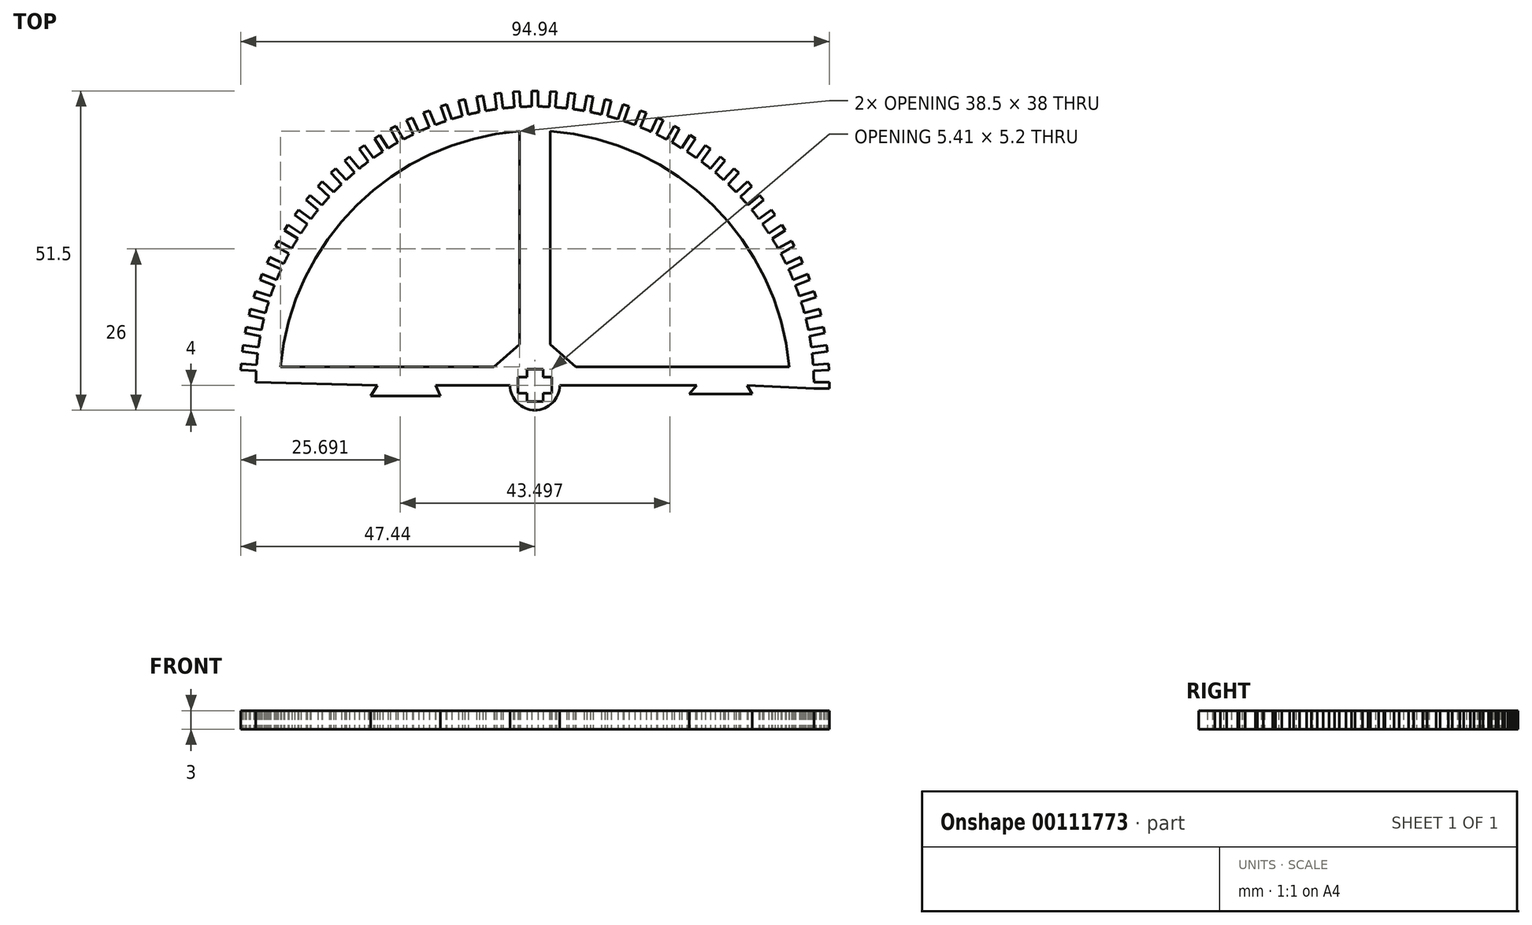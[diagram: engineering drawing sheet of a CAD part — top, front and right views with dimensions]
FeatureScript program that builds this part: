
annotation { "Feature Type Name" : "Feature", "Feature Type Description" : "" }
export const myFeature = defineFeature(function(context is Context, id is Id, definition is map)
    precondition{}
    {
        {
            var Q0;
            Q0=qCreatedBy(makeId("Top.planeOp"),FACE);
            var sketch = newSketch(context, id + "F0", { "sketchPlane" : qUnion([Q0])});
            skArc(sketch, "E0", {"start": v(-4, 0) * mm, "mid": v(0, -4) * mm, "end": v(4, 0) * mm});
            skLineSegment(sketch, "E1", {"start": v(-4, 0) * mm, "end": v(-16, 0) * mm});
            skLineSegment(sketch, "E2", {"start": v(-16, 0) * mm, "end": v(-15.27, -1.74) * mm});
            skLineSegment(sketch, "E3", {"start": v(-15.27, -1.74) * mm, "end": v(-26.47, -1.74) * mm});
            skLineSegment(sketch, "E4", {"start": v(-45, 0.5) * mm, "end": v(-25.37, 0) * mm});
            skLineSegment(sketch, "E5", {"start": v(-25.37, 0) * mm, "end": v(-26.47, -1.74) * mm});
            skLineSegment(sketch, "E6", {"start": v(45, -0.5) * mm, "end": v(34.22, 0) * mm});
            skLineSegment(sketch, "E7", {"start": v(34.22, 0) * mm, "end": v(35.03, -1.4) * mm});
            skLineSegment(sketch, "E8", {"start": v(35.03, -1.4) * mm, "end": v(24.89, -1.4) * mm});
            skLineSegment(sketch, "E9", {"start": v(24.89, -1.4) * mm, "end": v(26.1, 0) * mm});
            skLineSegment(sketch, "E10", {"start": v(26.1, 0) * mm, "end": v(4, 0) * mm});
            skArc(sketch, "E11", {"start": v(45, -0.5) * mm, "mid": v(0.5, 45) * mm, "end": v(-45, 0.5) * mm});
            skLineSegment(sketch, "E12.MirrorCS", {"start": v(-6.6, 3) * mm, "end": v(-41, 3) * mm});
            skLineSegment(sketch, "E13.MirrorCS", {"start": v(-2.5, 6.6) * mm, "end": v(-6.6, 3) * mm});
            skLineSegment(sketch, "E14.MirrorCS", {"start": v(-2.5, 6.6) * mm, "end": v(-2.5, 41) * mm});
            skArc(sketch, "E15.MirrorCS", {"start": v(-41, 3) * mm, "mid": v(-28.72, 29.07) * mm, "end": v(-2.5, 41) * mm});
            skLineSegment(sketch, "E16.MirrorCS", {"start": v(2.5, 6.6) * mm, "end": v(2.5, 41) * mm});
            skArc(sketch, "E17.MirrorCS", {"start": v(41, 3) * mm, "mid": v(28.72, 29.07) * mm, "end": v(2.5, 41) * mm});
            skLineSegment(sketch, "E18.MirrorCS", {"start": v(6.6, 3) * mm, "end": v(41, 3) * mm});
            skLineSegment(sketch, "E19.MirrorCS", {"start": v(2.5, 6.6) * mm, "end": v(6.6, 3) * mm});
            skLineSegment(sketch, "E20.1.50.0", {"start": v(47.5, 0.5) * mm, "end": v(45, 0.5) * mm});
            skLineSegment(sketch, "E20.3.50.0", {"start": v(47.5, -0.5) * mm, "end": v(45, -0.5) * mm});
            skLineSegment(sketch, "E20.6.50.0", {"start": v(47.5, 0) * mm, "end": v(47.5, -0.5) * mm});
            skLineSegment(sketch, "E20.9.50.0", {"start": v(47.5, 0) * mm, "end": v(47.5, 0.5) * mm});
            skLineSegment(sketch, "E20.1.51.0", {"start": v(47.37, 3.48) * mm, "end": v(44.88, 3.32) * mm});
            skLineSegment(sketch, "E20.3.51.0", {"start": v(47.44, 2.48) * mm, "end": v(44.94, 2.33) * mm});
            skLineSegment(sketch, "E20.6.51.0", {"start": v(47.4, 2.98) * mm, "end": v(47.44, 2.48) * mm});
            skLineSegment(sketch, "E20.9.51.0", {"start": v(47.4, 2.98) * mm, "end": v(47.37, 3.48) * mm});
            skLineSegment(sketch, "E20.1.52.0", {"start": v(47.06, 6.45) * mm, "end": v(44.58, 6.14) * mm});
            skLineSegment(sketch, "E20.3.52.0", {"start": v(47.19, 5.46) * mm, "end": v(44.7, 5.14) * mm});
            skLineSegment(sketch, "E20.6.52.0", {"start": v(47.13, 5.95) * mm, "end": v(47.19, 5.46) * mm});
            skLineSegment(sketch, "E20.9.52.0", {"start": v(47.13, 5.95) * mm, "end": v(47.06, 6.45) * mm});
            skLineSegment(sketch, "E20.1.53.0", {"start": v(46.56, 9.4) * mm, "end": v(44.1, 8.92) * mm});
            skLineSegment(sketch, "E20.3.53.0", {"start": v(46.75, 8.4) * mm, "end": v(44.3, 7.94) * mm});
            skLineSegment(sketch, "E20.6.53.0", {"start": v(46.66, 8.9) * mm, "end": v(46.75, 8.4) * mm});
            skLineSegment(sketch, "E20.9.53.0", {"start": v(46.66, 8.9) * mm, "end": v(46.56, 9.4) * mm});
            skLineSegment(sketch, "E20.1.54.0", {"start": v(45.88, 12.3) * mm, "end": v(43.46, 11.67) * mm});
            skLineSegment(sketch, "E20.3.54.0", {"start": v(46.13, 11.33) * mm, "end": v(43.7, 10.7) * mm});
            skLineSegment(sketch, "E20.6.54.0", {"start": v(46, 11.81) * mm, "end": v(46.13, 11.33) * mm});
            skLineSegment(sketch, "E20.9.54.0", {"start": v(46, 11.81) * mm, "end": v(45.88, 12.3) * mm});
            skLineSegment(sketch, "E20.1.55.0", {"start": v(45.02, 15.15) * mm, "end": v(42.64, 14.38) * mm});
            skLineSegment(sketch, "E20.3.55.0", {"start": v(45.33, 14.2) * mm, "end": v(42.95, 13.43) * mm});
            skLineSegment(sketch, "E20.6.55.0", {"start": v(45.18, 14.68) * mm, "end": v(45.33, 14.2) * mm});
            skLineSegment(sketch, "E20.9.55.0", {"start": v(45.18, 14.68) * mm, "end": v(45.02, 15.15) * mm});
            skLineSegment(sketch, "E20.1.56.0", {"start": v(43.98, 17.95) * mm, "end": v(41.65, 17.03) * mm});
            skLineSegment(sketch, "E20.3.56.0", {"start": v(44.35, 17.02) * mm, "end": v(42.02, 16.1) * mm});
            skLineSegment(sketch, "E20.6.56.0", {"start": v(44.16, 17.49) * mm, "end": v(44.35, 17.02) * mm});
            skLineSegment(sketch, "E20.9.56.0", {"start": v(44.16, 17.49) * mm, "end": v(43.98, 17.95) * mm});
            skLineSegment(sketch, "E20.1.57.0", {"start": v(42.77, 20.68) * mm, "end": v(40.5, 19.61) * mm});
            skLineSegment(sketch, "E20.3.57.0", {"start": v(43.2, 19.77) * mm, "end": v(40.93, 18.7) * mm});
            skLineSegment(sketch, "E20.6.57.0", {"start": v(42.98, 20.22) * mm, "end": v(43.2, 19.77) * mm});
            skLineSegment(sketch, "E20.9.57.0", {"start": v(42.98, 20.22) * mm, "end": v(42.77, 20.68) * mm});
            skLineSegment(sketch, "E20.1.58.0", {"start": v(41.38, 23.32) * mm, "end": v(39.2, 22.12) * mm});
            skLineSegment(sketch, "E20.3.58.0", {"start": v(41.87, 22.45) * mm, "end": v(39.67, 21.24) * mm});
            skLineSegment(sketch, "E20.6.58.0", {"start": v(41.62, 22.88) * mm, "end": v(41.87, 22.45) * mm});
            skLineSegment(sketch, "E20.9.58.0", {"start": v(41.62, 22.88) * mm, "end": v(41.38, 23.32) * mm});
            skLineSegment(sketch, "E20.1.59.0", {"start": v(39.84, 25.87) * mm, "end": v(37.72, 24.53) * mm});
            skLineSegment(sketch, "E20.3.59.0", {"start": v(40.37, 25.03) * mm, "end": v(38.26, 23.69) * mm});
            skLineSegment(sketch, "E20.6.59.0", {"start": v(40.1, 25.45) * mm, "end": v(40.37, 25.03) * mm});
            skLineSegment(sketch, "E20.9.59.0", {"start": v(40.1, 25.45) * mm, "end": v(39.84, 25.87) * mm});
            skLineSegment(sketch, "E20.1.60.0", {"start": v(38.13, 28.32) * mm, "end": v(36.1, 26.85) * mm});
            skLineSegment(sketch, "E20.3.60.0", {"start": v(38.72, 27.52) * mm, "end": v(36.7, 26.04) * mm});
            skLineSegment(sketch, "E20.6.60.0", {"start": v(38.43, 27.92) * mm, "end": v(38.72, 27.52) * mm});
            skLineSegment(sketch, "E20.9.60.0", {"start": v(38.43, 27.92) * mm, "end": v(38.13, 28.32) * mm});
            skLineSegment(sketch, "E20.1.61.0", {"start": v(36.28, 30.66) * mm, "end": v(34.35, 29.07) * mm});
            skLineSegment(sketch, "E20.3.61.0", {"start": v(36.92, 29.9) * mm, "end": v(34.99, 28.3) * mm});
            skLineSegment(sketch, "E20.6.61.0", {"start": v(36.6, 30.28) * mm, "end": v(36.92, 29.9) * mm});
            skLineSegment(sketch, "E20.9.61.0", {"start": v(36.6, 30.28) * mm, "end": v(36.28, 30.66) * mm});
            skLineSegment(sketch, "E20.1.62.0", {"start": v(34.28, 32.88) * mm, "end": v(32.46, 31.17) * mm});
            skLineSegment(sketch, "E20.3.62.0", {"start": v(34.97, 32.15) * mm, "end": v(33.14, 30.44) * mm});
            skLineSegment(sketch, "E20.6.62.0", {"start": v(34.63, 32.52) * mm, "end": v(34.97, 32.15) * mm});
            skLineSegment(sketch, "E20.9.62.0", {"start": v(34.63, 32.52) * mm, "end": v(34.28, 32.88) * mm});
            skLineSegment(sketch, "E20.1.63.0", {"start": v(32.15, 34.97) * mm, "end": v(30.44, 33.14) * mm});
            skLineSegment(sketch, "E20.3.63.0", {"start": v(32.88, 34.28) * mm, "end": v(31.17, 32.46) * mm});
            skLineSegment(sketch, "E20.6.63.0", {"start": v(32.52, 34.63) * mm, "end": v(32.88, 34.28) * mm});
            skLineSegment(sketch, "E20.9.63.0", {"start": v(32.52, 34.63) * mm, "end": v(32.15, 34.97) * mm});
            skLineSegment(sketch, "E20.1.64.0", {"start": v(29.9, 36.92) * mm, "end": v(28.3, 34.99) * mm});
            skLineSegment(sketch, "E20.3.64.0", {"start": v(30.66, 36.28) * mm, "end": v(29.07, 34.35) * mm});
            skLineSegment(sketch, "E20.6.64.0", {"start": v(30.28, 36.6) * mm, "end": v(30.66, 36.28) * mm});
            skLineSegment(sketch, "E20.9.64.0", {"start": v(30.28, 36.6) * mm, "end": v(29.9, 36.92) * mm});
            skLineSegment(sketch, "E20.1.65.0", {"start": v(27.52, 38.72) * mm, "end": v(26.04, 36.7) * mm});
            skLineSegment(sketch, "E20.3.65.0", {"start": v(28.32, 38.13) * mm, "end": v(26.85, 36.1) * mm});
            skLineSegment(sketch, "E20.6.65.0", {"start": v(27.92, 38.43) * mm, "end": v(28.32, 38.13) * mm});
            skLineSegment(sketch, "E20.9.65.0", {"start": v(27.92, 38.43) * mm, "end": v(27.52, 38.72) * mm});
            skLineSegment(sketch, "E20.1.66.0", {"start": v(25.03, 40.37) * mm, "end": v(23.69, 38.26) * mm});
            skLineSegment(sketch, "E20.3.66.0", {"start": v(25.87, 39.84) * mm, "end": v(24.53, 37.72) * mm});
            skLineSegment(sketch, "E20.6.66.0", {"start": v(25.45, 40.1) * mm, "end": v(25.87, 39.84) * mm});
            skLineSegment(sketch, "E20.9.66.0", {"start": v(25.45, 40.1) * mm, "end": v(25.03, 40.37) * mm});
            skLineSegment(sketch, "E20.1.67.0", {"start": v(22.45, 41.87) * mm, "end": v(21.24, 39.67) * mm});
            skLineSegment(sketch, "E20.3.67.0", {"start": v(23.32, 41.38) * mm, "end": v(22.12, 39.2) * mm});
            skLineSegment(sketch, "E20.6.67.0", {"start": v(22.88, 41.62) * mm, "end": v(23.32, 41.38) * mm});
            skLineSegment(sketch, "E20.9.67.0", {"start": v(22.88, 41.62) * mm, "end": v(22.45, 41.87) * mm});
            skLineSegment(sketch, "E20.1.68.0", {"start": v(19.77, 43.2) * mm, "end": v(18.7, 40.93) * mm});
            skLineSegment(sketch, "E20.3.68.0", {"start": v(20.68, 42.77) * mm, "end": v(19.61, 40.5) * mm});
            skLineSegment(sketch, "E20.6.68.0", {"start": v(20.22, 42.98) * mm, "end": v(20.68, 42.77) * mm});
            skLineSegment(sketch, "E20.9.68.0", {"start": v(20.22, 42.98) * mm, "end": v(19.77, 43.2) * mm});
            skLineSegment(sketch, "E20.1.69.0", {"start": v(17.02, 44.35) * mm, "end": v(16.1, 42.02) * mm});
            skLineSegment(sketch, "E20.3.69.0", {"start": v(17.95, 43.98) * mm, "end": v(17.03, 41.65) * mm});
            skLineSegment(sketch, "E20.6.69.0", {"start": v(17.49, 44.16) * mm, "end": v(17.95, 43.98) * mm});
            skLineSegment(sketch, "E20.9.69.0", {"start": v(17.49, 44.16) * mm, "end": v(17.02, 44.35) * mm});
            skLineSegment(sketch, "E20.1.70.0", {"start": v(14.2, 45.33) * mm, "end": v(13.43, 42.95) * mm});
            skLineSegment(sketch, "E20.3.70.0", {"start": v(15.15, 45.02) * mm, "end": v(14.38, 42.64) * mm});
            skLineSegment(sketch, "E20.6.70.0", {"start": v(14.68, 45.18) * mm, "end": v(15.15, 45.02) * mm});
            skLineSegment(sketch, "E20.9.70.0", {"start": v(14.68, 45.18) * mm, "end": v(14.2, 45.33) * mm});
            skLineSegment(sketch, "E20.1.71.0", {"start": v(11.33, 46.13) * mm, "end": v(10.7, 43.7) * mm});
            skLineSegment(sketch, "E20.3.71.0", {"start": v(12.3, 45.88) * mm, "end": v(11.67, 43.46) * mm});
            skLineSegment(sketch, "E20.6.71.0", {"start": v(11.81, 46) * mm, "end": v(12.3, 45.88) * mm});
            skLineSegment(sketch, "E20.9.71.0", {"start": v(11.81, 46) * mm, "end": v(11.33, 46.13) * mm});
            skLineSegment(sketch, "E20.1.72.0", {"start": v(8.4, 46.75) * mm, "end": v(7.94, 44.3) * mm});
            skLineSegment(sketch, "E20.3.72.0", {"start": v(9.4, 46.56) * mm, "end": v(8.92, 44.1) * mm});
            skLineSegment(sketch, "E20.6.72.0", {"start": v(8.9, 46.66) * mm, "end": v(9.4, 46.56) * mm});
            skLineSegment(sketch, "E20.9.72.0", {"start": v(8.9, 46.66) * mm, "end": v(8.4, 46.75) * mm});
            skLineSegment(sketch, "E20.1.73.0", {"start": v(5.46, 47.19) * mm, "end": v(5.14, 44.7) * mm});
            skLineSegment(sketch, "E20.3.73.0", {"start": v(6.45, 47.06) * mm, "end": v(6.14, 44.58) * mm});
            skLineSegment(sketch, "E20.6.73.0", {"start": v(5.95, 47.13) * mm, "end": v(6.45, 47.06) * mm});
            skLineSegment(sketch, "E20.9.73.0", {"start": v(5.95, 47.13) * mm, "end": v(5.46, 47.19) * mm});
            skLineSegment(sketch, "E20.1.74.0", {"start": v(2.48, 47.44) * mm, "end": v(2.33, 44.94) * mm});
            skLineSegment(sketch, "E20.3.74.0", {"start": v(3.48, 47.37) * mm, "end": v(3.32, 44.88) * mm});
            skLineSegment(sketch, "E20.6.74.0", {"start": v(2.98, 47.4) * mm, "end": v(3.48, 47.37) * mm});
            skLineSegment(sketch, "E20.9.74.0", {"start": v(2.98, 47.4) * mm, "end": v(2.48, 47.44) * mm});
            skLineSegment(sketch, "E20.1.75.0", {"start": v(-0.5, 47.5) * mm, "end": v(-0.5, 45) * mm});
            skLineSegment(sketch, "E20.3.75.0", {"start": v(0.5, 47.5) * mm, "end": v(0.5, 45) * mm});
            skLineSegment(sketch, "E20.6.75.0", {"start": v(0, 47.5) * mm, "end": v(0.5, 47.5) * mm});
            skLineSegment(sketch, "E20.9.75.0", {"start": v(0, 47.5) * mm, "end": v(-0.5, 47.5) * mm});
            skLineSegment(sketch, "E20.1.76.0", {"start": v(-3.48, 47.37) * mm, "end": v(-3.32, 44.88) * mm});
            skLineSegment(sketch, "E20.3.76.0", {"start": v(-2.48, 47.44) * mm, "end": v(-2.33, 44.94) * mm});
            skLineSegment(sketch, "E20.6.76.0", {"start": v(-2.98, 47.4) * mm, "end": v(-2.48, 47.44) * mm});
            skLineSegment(sketch, "E20.9.76.0", {"start": v(-2.98, 47.4) * mm, "end": v(-3.48, 47.37) * mm});
            skLineSegment(sketch, "E20.1.77.0", {"start": v(-6.45, 47.06) * mm, "end": v(-6.14, 44.58) * mm});
            skLineSegment(sketch, "E20.3.77.0", {"start": v(-5.46, 47.19) * mm, "end": v(-5.14, 44.7) * mm});
            skLineSegment(sketch, "E20.6.77.0", {"start": v(-5.95, 47.13) * mm, "end": v(-5.46, 47.19) * mm});
            skLineSegment(sketch, "E20.9.77.0", {"start": v(-5.95, 47.13) * mm, "end": v(-6.45, 47.06) * mm});
            skLineSegment(sketch, "E20.1.78.0", {"start": v(-9.4, 46.56) * mm, "end": v(-8.92, 44.1) * mm});
            skLineSegment(sketch, "E20.3.78.0", {"start": v(-8.4, 46.75) * mm, "end": v(-7.94, 44.3) * mm});
            skLineSegment(sketch, "E20.6.78.0", {"start": v(-8.9, 46.66) * mm, "end": v(-8.4, 46.75) * mm});
            skLineSegment(sketch, "E20.9.78.0", {"start": v(-8.9, 46.66) * mm, "end": v(-9.4, 46.56) * mm});
            skLineSegment(sketch, "E20.1.79.0", {"start": v(-12.3, 45.88) * mm, "end": v(-11.67, 43.46) * mm});
            skLineSegment(sketch, "E20.3.79.0", {"start": v(-11.33, 46.13) * mm, "end": v(-10.7, 43.7) * mm});
            skLineSegment(sketch, "E20.6.79.0", {"start": v(-11.81, 46) * mm, "end": v(-11.33, 46.13) * mm});
            skLineSegment(sketch, "E20.9.79.0", {"start": v(-11.81, 46) * mm, "end": v(-12.3, 45.88) * mm});
            skLineSegment(sketch, "E20.1.80.0", {"start": v(-15.15, 45.02) * mm, "end": v(-14.38, 42.64) * mm});
            skLineSegment(sketch, "E20.3.80.0", {"start": v(-14.2, 45.33) * mm, "end": v(-13.43, 42.95) * mm});
            skLineSegment(sketch, "E20.6.80.0", {"start": v(-14.68, 45.18) * mm, "end": v(-14.2, 45.33) * mm});
            skLineSegment(sketch, "E20.9.80.0", {"start": v(-14.68, 45.18) * mm, "end": v(-15.15, 45.02) * mm});
            skLineSegment(sketch, "E20.1.81.0", {"start": v(-17.95, 43.98) * mm, "end": v(-17.03, 41.65) * mm});
            skLineSegment(sketch, "E20.3.81.0", {"start": v(-17.02, 44.35) * mm, "end": v(-16.1, 42.02) * mm});
            skLineSegment(sketch, "E20.6.81.0", {"start": v(-17.49, 44.16) * mm, "end": v(-17.02, 44.35) * mm});
            skLineSegment(sketch, "E20.9.81.0", {"start": v(-17.49, 44.16) * mm, "end": v(-17.95, 43.98) * mm});
            skLineSegment(sketch, "E20.1.82.0", {"start": v(-20.68, 42.77) * mm, "end": v(-19.61, 40.5) * mm});
            skLineSegment(sketch, "E20.3.82.0", {"start": v(-19.77, 43.2) * mm, "end": v(-18.7, 40.93) * mm});
            skLineSegment(sketch, "E20.6.82.0", {"start": v(-20.22, 42.98) * mm, "end": v(-19.77, 43.2) * mm});
            skLineSegment(sketch, "E20.9.82.0", {"start": v(-20.22, 42.98) * mm, "end": v(-20.68, 42.77) * mm});
            skLineSegment(sketch, "E20.1.83.0", {"start": v(-23.32, 41.38) * mm, "end": v(-22.12, 39.2) * mm});
            skLineSegment(sketch, "E20.3.83.0", {"start": v(-22.45, 41.87) * mm, "end": v(-21.24, 39.67) * mm});
            skLineSegment(sketch, "E20.6.83.0", {"start": v(-22.88, 41.62) * mm, "end": v(-22.45, 41.87) * mm});
            skLineSegment(sketch, "E20.9.83.0", {"start": v(-22.88, 41.62) * mm, "end": v(-23.32, 41.38) * mm});
            skLineSegment(sketch, "E20.1.84.0", {"start": v(-25.87, 39.84) * mm, "end": v(-24.53, 37.72) * mm});
            skLineSegment(sketch, "E20.3.84.0", {"start": v(-25.03, 40.37) * mm, "end": v(-23.69, 38.26) * mm});
            skLineSegment(sketch, "E20.6.84.0", {"start": v(-25.45, 40.1) * mm, "end": v(-25.03, 40.37) * mm});
            skLineSegment(sketch, "E20.9.84.0", {"start": v(-25.45, 40.1) * mm, "end": v(-25.87, 39.84) * mm});
            skLineSegment(sketch, "E20.1.85.0", {"start": v(-28.32, 38.13) * mm, "end": v(-26.85, 36.1) * mm});
            skLineSegment(sketch, "E20.3.85.0", {"start": v(-27.52, 38.72) * mm, "end": v(-26.04, 36.7) * mm});
            skLineSegment(sketch, "E20.6.85.0", {"start": v(-27.92, 38.43) * mm, "end": v(-27.52, 38.72) * mm});
            skLineSegment(sketch, "E20.9.85.0", {"start": v(-27.92, 38.43) * mm, "end": v(-28.32, 38.13) * mm});
            skLineSegment(sketch, "E20.1.86.0", {"start": v(-30.66, 36.28) * mm, "end": v(-29.07, 34.35) * mm});
            skLineSegment(sketch, "E20.3.86.0", {"start": v(-29.9, 36.92) * mm, "end": v(-28.3, 34.99) * mm});
            skLineSegment(sketch, "E20.6.86.0", {"start": v(-30.28, 36.6) * mm, "end": v(-29.9, 36.92) * mm});
            skLineSegment(sketch, "E20.9.86.0", {"start": v(-30.28, 36.6) * mm, "end": v(-30.66, 36.28) * mm});
            skLineSegment(sketch, "E20.1.87.0", {"start": v(-32.88, 34.28) * mm, "end": v(-31.17, 32.46) * mm});
            skLineSegment(sketch, "E20.3.87.0", {"start": v(-32.15, 34.97) * mm, "end": v(-30.44, 33.14) * mm});
            skLineSegment(sketch, "E20.6.87.0", {"start": v(-32.52, 34.63) * mm, "end": v(-32.15, 34.97) * mm});
            skLineSegment(sketch, "E20.9.87.0", {"start": v(-32.52, 34.63) * mm, "end": v(-32.88, 34.28) * mm});
            skLineSegment(sketch, "E20.1.88.0", {"start": v(-34.97, 32.15) * mm, "end": v(-33.14, 30.44) * mm});
            skLineSegment(sketch, "E20.3.88.0", {"start": v(-34.28, 32.88) * mm, "end": v(-32.46, 31.17) * mm});
            skLineSegment(sketch, "E20.6.88.0", {"start": v(-34.63, 32.52) * mm, "end": v(-34.28, 32.88) * mm});
            skLineSegment(sketch, "E20.9.88.0", {"start": v(-34.63, 32.52) * mm, "end": v(-34.97, 32.15) * mm});
            skLineSegment(sketch, "E20.1.89.0", {"start": v(-36.92, 29.9) * mm, "end": v(-34.99, 28.3) * mm});
            skLineSegment(sketch, "E20.3.89.0", {"start": v(-36.28, 30.66) * mm, "end": v(-34.35, 29.07) * mm});
            skLineSegment(sketch, "E20.6.89.0", {"start": v(-36.6, 30.28) * mm, "end": v(-36.28, 30.66) * mm});
            skLineSegment(sketch, "E20.9.89.0", {"start": v(-36.6, 30.28) * mm, "end": v(-36.92, 29.9) * mm});
            skLineSegment(sketch, "E20.1.90.0", {"start": v(-38.72, 27.52) * mm, "end": v(-36.7, 26.04) * mm});
            skLineSegment(sketch, "E20.3.90.0", {"start": v(-38.13, 28.32) * mm, "end": v(-36.1, 26.85) * mm});
            skLineSegment(sketch, "E20.6.90.0", {"start": v(-38.43, 27.92) * mm, "end": v(-38.13, 28.32) * mm});
            skLineSegment(sketch, "E20.9.90.0", {"start": v(-38.43, 27.92) * mm, "end": v(-38.72, 27.52) * mm});
            skLineSegment(sketch, "E20.1.91.0", {"start": v(-40.37, 25.03) * mm, "end": v(-38.26, 23.69) * mm});
            skLineSegment(sketch, "E20.3.91.0", {"start": v(-39.84, 25.87) * mm, "end": v(-37.72, 24.53) * mm});
            skLineSegment(sketch, "E20.6.91.0", {"start": v(-40.1, 25.45) * mm, "end": v(-39.84, 25.87) * mm});
            skLineSegment(sketch, "E20.9.91.0", {"start": v(-40.1, 25.45) * mm, "end": v(-40.37, 25.03) * mm});
            skLineSegment(sketch, "E20.1.92.0", {"start": v(-41.87, 22.45) * mm, "end": v(-39.67, 21.24) * mm});
            skLineSegment(sketch, "E20.3.92.0", {"start": v(-41.38, 23.32) * mm, "end": v(-39.2, 22.12) * mm});
            skLineSegment(sketch, "E20.6.92.0", {"start": v(-41.62, 22.88) * mm, "end": v(-41.38, 23.32) * mm});
            skLineSegment(sketch, "E20.9.92.0", {"start": v(-41.62, 22.88) * mm, "end": v(-41.87, 22.45) * mm});
            skLineSegment(sketch, "E20.1.93.0", {"start": v(-43.2, 19.77) * mm, "end": v(-40.93, 18.7) * mm});
            skLineSegment(sketch, "E20.3.93.0", {"start": v(-42.77, 20.68) * mm, "end": v(-40.5, 19.61) * mm});
            skLineSegment(sketch, "E20.6.93.0", {"start": v(-42.98, 20.22) * mm, "end": v(-42.77, 20.68) * mm});
            skLineSegment(sketch, "E20.9.93.0", {"start": v(-42.98, 20.22) * mm, "end": v(-43.2, 19.77) * mm});
            skLineSegment(sketch, "E20.1.94.0", {"start": v(-44.35, 17.02) * mm, "end": v(-42.02, 16.1) * mm});
            skLineSegment(sketch, "E20.3.94.0", {"start": v(-43.98, 17.95) * mm, "end": v(-41.65, 17.03) * mm});
            skLineSegment(sketch, "E20.6.94.0", {"start": v(-44.16, 17.49) * mm, "end": v(-43.98, 17.95) * mm});
            skLineSegment(sketch, "E20.9.94.0", {"start": v(-44.16, 17.49) * mm, "end": v(-44.35, 17.02) * mm});
            skLineSegment(sketch, "E20.1.95.0", {"start": v(-45.33, 14.2) * mm, "end": v(-42.95, 13.43) * mm});
            skLineSegment(sketch, "E20.3.95.0", {"start": v(-45.02, 15.15) * mm, "end": v(-42.64, 14.38) * mm});
            skLineSegment(sketch, "E20.6.95.0", {"start": v(-45.18, 14.68) * mm, "end": v(-45.02, 15.15) * mm});
            skLineSegment(sketch, "E20.9.95.0", {"start": v(-45.18, 14.68) * mm, "end": v(-45.33, 14.2) * mm});
            skLineSegment(sketch, "E20.1.96.0", {"start": v(-46.13, 11.33) * mm, "end": v(-43.7, 10.7) * mm});
            skLineSegment(sketch, "E20.3.96.0", {"start": v(-45.88, 12.3) * mm, "end": v(-43.46, 11.67) * mm});
            skLineSegment(sketch, "E20.6.96.0", {"start": v(-46, 11.81) * mm, "end": v(-45.88, 12.3) * mm});
            skLineSegment(sketch, "E20.9.96.0", {"start": v(-46, 11.81) * mm, "end": v(-46.13, 11.33) * mm});
            skLineSegment(sketch, "E20.1.97.0", {"start": v(-46.75, 8.4) * mm, "end": v(-44.3, 7.94) * mm});
            skLineSegment(sketch, "E20.3.97.0", {"start": v(-46.56, 9.4) * mm, "end": v(-44.1, 8.92) * mm});
            skLineSegment(sketch, "E20.6.97.0", {"start": v(-46.66, 8.9) * mm, "end": v(-46.56, 9.4) * mm});
            skLineSegment(sketch, "E20.9.97.0", {"start": v(-46.66, 8.9) * mm, "end": v(-46.75, 8.4) * mm});
            skLineSegment(sketch, "E20.1.98.0", {"start": v(-47.19, 5.46) * mm, "end": v(-44.7, 5.14) * mm});
            skLineSegment(sketch, "E20.3.98.0", {"start": v(-47.06, 6.45) * mm, "end": v(-44.58, 6.14) * mm});
            skLineSegment(sketch, "E20.6.98.0", {"start": v(-47.13, 5.95) * mm, "end": v(-47.06, 6.45) * mm});
            skLineSegment(sketch, "E20.9.98.0", {"start": v(-47.13, 5.95) * mm, "end": v(-47.19, 5.46) * mm});
            skLineSegment(sketch, "E20.1.99.0", {"start": v(-47.44, 2.48) * mm, "end": v(-44.94, 2.33) * mm});
            skLineSegment(sketch, "E20.3.99.0", {"start": v(-47.37, 3.48) * mm, "end": v(-44.88, 3.32) * mm});
            skLineSegment(sketch, "E20.6.99.0", {"start": v(-47.4, 2.98) * mm, "end": v(-47.37, 3.48) * mm});
            skLineSegment(sketch, "E20.9.99.0", {"start": v(-47.4, 2.98) * mm, "end": v(-47.44, 2.48) * mm});
            skLineSegment(sketch, "E21", {"start": v(0, 2.6) * mm, "end": v(1.3, 2.6) * mm});
            skLineSegment(sketch, "E22", {"start": v(1.3, 2.6) * mm, "end": v(1.3, 1.3) * mm});
            skLineSegment(sketch, "E23", {"start": v(1.3, 1.3) * mm, "end": v(2.7, 1.3) * mm});
            skLineSegment(sketch, "E24", {"start": v(2.7, 1.3) * mm, "end": v(2.7, 0) * mm});
            skLineSegment(sketch, "E25.MirrorCS", {"start": v(0, 2.6) * mm, "end": v(-1.3, 2.6) * mm});
            skLineSegment(sketch, "E26.MirrorCS", {"start": v(-1.3, 2.6) * mm, "end": v(-1.3, 1.3) * mm});
            skLineSegment(sketch, "E27.MirrorCS", {"start": v(-1.3, 1.3) * mm, "end": v(-2.7, 1.3) * mm});
            skLineSegment(sketch, "E28.MirrorCS", {"start": v(-2.7, 1.3) * mm, "end": v(-2.7, 0) * mm});
            skLineSegment(sketch, "E29.MirrorCS", {"start": v(-2.7, -1.3) * mm, "end": v(-2.7, 0) * mm});
            skLineSegment(sketch, "E30.MirrorCS", {"start": v(-1.3, -1.3) * mm, "end": v(-2.7, -1.3) * mm});
            skLineSegment(sketch, "E31.MirrorCS", {"start": v(-1.3, -2.6) * mm, "end": v(-1.3, -1.3) * mm});
            skLineSegment(sketch, "E32.MirrorCS", {"start": v(0, -2.6) * mm, "end": v(-1.3, -2.6) * mm});
            skLineSegment(sketch, "E33.MirrorCS", {"start": v(0, -2.6) * mm, "end": v(1.3, -2.6) * mm});
            skLineSegment(sketch, "E34.MirrorCS", {"start": v(1.3, -2.6) * mm, "end": v(1.3, -1.3) * mm});
            skLineSegment(sketch, "E35.MirrorCS", {"start": v(1.3, -1.3) * mm, "end": v(2.7, -1.3) * mm});
            skLineSegment(sketch, "E36.MirrorCS", {"start": v(2.7, -1.3) * mm, "end": v(2.7, 0) * mm});
            skSolve(sketch);
        }
        {
            var Q0;
            Q0=qSketchRegion(id+"F0",true);
            extrude(context, id + "F1", {"entities" : qUnion([Q0]), "depth" : 3 * mm});
        }
    });
